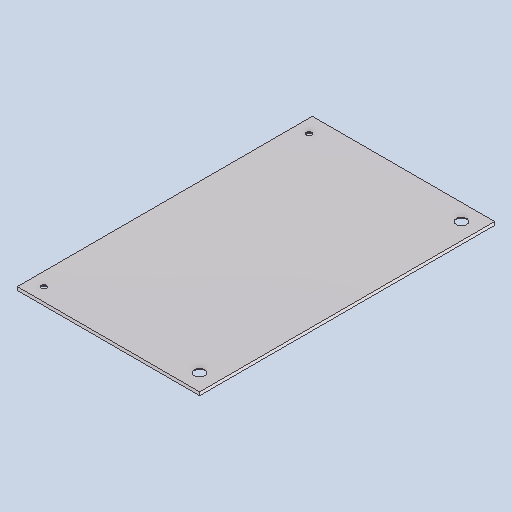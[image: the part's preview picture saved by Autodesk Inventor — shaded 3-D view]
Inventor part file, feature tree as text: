
AUTODESK INVENTOR PART (.ipt)
format: ipt  version: 2025 (Build 290162010, 162A)  size: 165,376 bytes
history: native  units: mm
features: hole x2, sketch x2, other x1
ambient origin geometry x8: Origin, YZ Plane, XZ Plane, XY Plane, X Axis, Y Axis, Z Axis, Center Point
bodies: Volumenkörper1 (feature_tree)
feature tree (5):
  hole  "Bohrung1"  [1 undecoded]
  hole  "Bohrung2"  [1 undecoded]
  sketch  "Skizze1"  dims[d1=10.0mm]
  sketch  "Skizze2"  dims[d2=5.3mm d3=6.0mm d4=10.4mm d5=2.0mm d6=90.0deg d7=8.0mm d8=20.594885mm d9=8.0mm d10=8.0mm d11=10.0mm d12=3.2mm d13=6.0mm d14=6.3mm d15=2.0mm d16=90.0deg d17=8.0mm d18=20.594885mm]
  other  "item_47308_blech-al-2mm-naturfarben_178_110_high_1_1:1"
note: 2 required parameter values undecoded (feature->parameter linkage not recoverable at this tier; creation-order binding heuristic only, values carry confidence <= 0.55)
